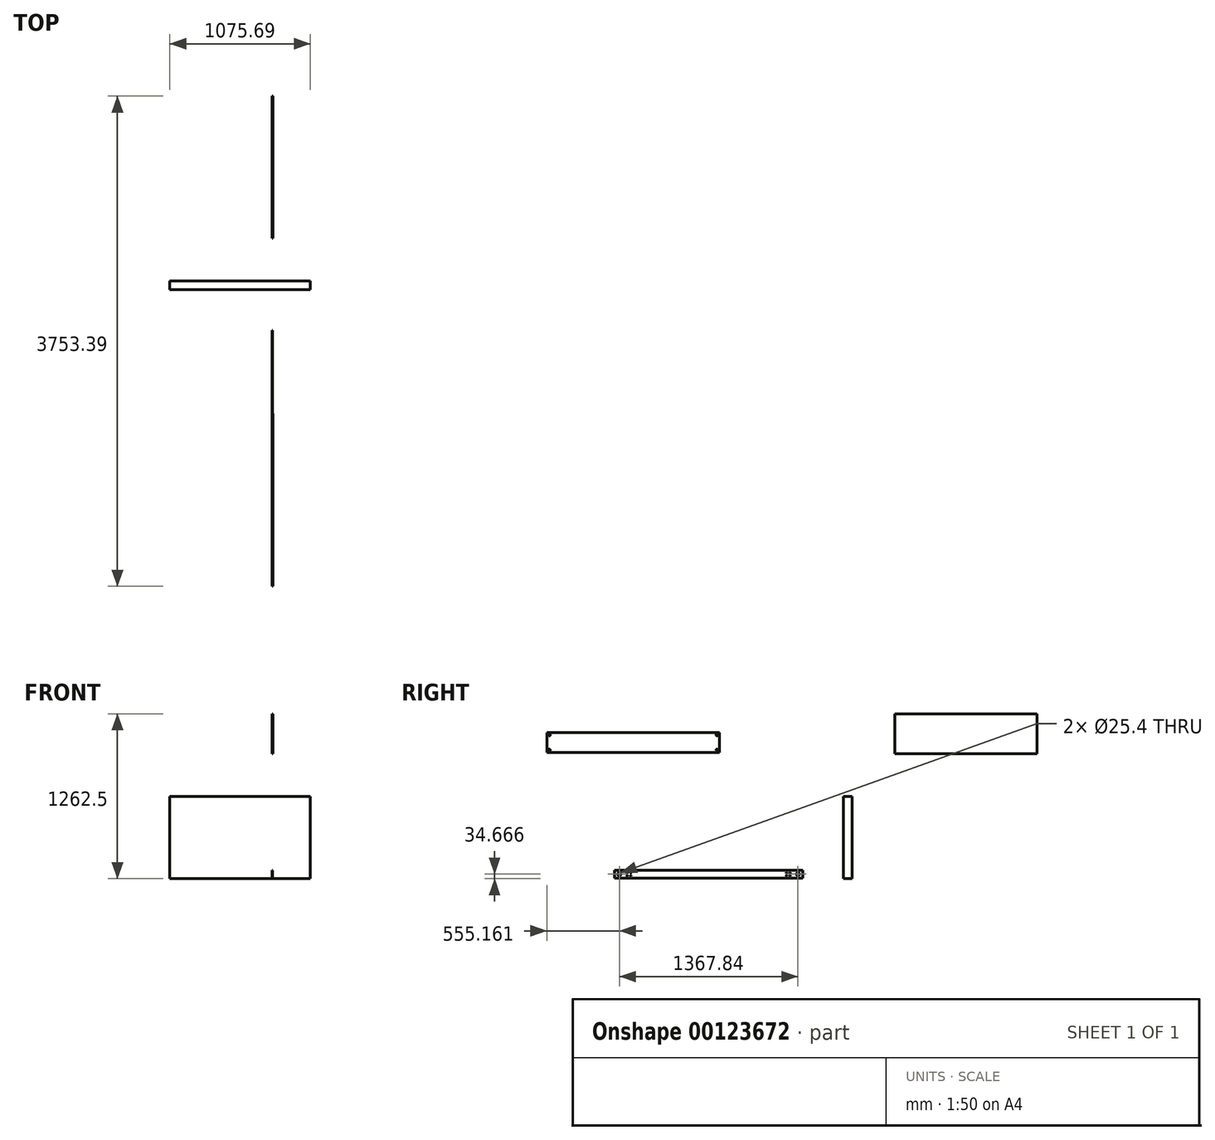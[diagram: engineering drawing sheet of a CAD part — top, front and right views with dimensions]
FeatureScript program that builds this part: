
annotation { "Feature Type Name" : "Feature", "Feature Type Description" : "" }
export const myFeature = defineFeature(function(context is Context, id is Id, definition is map)
    precondition{}
    {
        {
            var Q0;
            Q0=qCreatedBy(makeId("Front.planeOp"),FACE);
            var sketch = newSketch(context, id + "F0", { "sketchPlane" : qUnion([Q0])});
            skLineSegment(sketch, "E0.bottom", {"start": v(-783.94, 247.8) * mm, "end": v(291.75, 247.8) * mm});
            skLineSegment(sketch, "E0.top", {"start": v(-783.94, -380.85) * mm, "end": v(291.75, -380.85) * mm});
            skLineSegment(sketch, "E0.left", {"start": v(-783.94, 247.8) * mm, "end": v(-783.94, -380.85) * mm});
            skLineSegment(sketch, "E0.right", {"start": v(291.75, 247.8) * mm, "end": v(291.75, -380.85) * mm});
            skSolve(sketch);
        }
        {
            var Q0;
            Q0=makeQuery(id+"F0.imprint","IMPRINT",FACE,{"disambiguationData":[TD([[makeQuery(id+"F0.imprint","IMPRINT",EDGE,{"derivedFrom":sQuery(id+"F0.wireOp",EDGE,"E0.bottom")}),-1.0]])]});
            extrude(context, id + "F1", {"entities" : qUnion([Q0]), "depth" : 67.3 * mm});
        }
        {
            var Q0;
            Q0=qCreatedBy(makeId("Right.planeOp"),FACE);
            var sketch = newSketch(context, id + "F2", { "sketchPlane" : qUnion([Q0])});
            skLineSegment(sketch, "E1.bottom", {"start": v(325.72, 881.65) * mm, "end": v(1414.1, 881.65) * mm});
            skLineSegment(sketch, "E1.top", {"start": v(325.72, 576.85) * mm, "end": v(1414.1, 576.85) * mm});
            skLineSegment(sketch, "E1.left", {"start": v(325.72, 881.65) * mm, "end": v(325.72, 576.85) * mm});
            skLineSegment(sketch, "E1.right", {"start": v(1414.1, 881.65) * mm, "end": v(1414.1, 576.85) * mm});
            skSolve(sketch);
        }
        {
            var Q0;
            Q0=makeQuery(id+"F2.imprint","IMPRINT",FACE,{"disambiguationData":[TD([[makeQuery(id+"F2.imprint","IMPRINT",EDGE,{"derivedFrom":sQuery(id+"F2.wireOp",EDGE,"E1.bottom")}),-1.0]])]});
            extrude(context, id + "F3", {"entities" : qUnion([Q0]), "depth" : 6.35 * mm});
        }
        {
            var Q0;
            Q0=qCreatedBy(makeId("Right.planeOp"),FACE);
            var sketch = newSketch(context, id + "F4", { "sketchPlane" : qUnion([Q0])});
            skLineSegment(sketch, "E2.bottom", {"start": v(-2339.28, 737.4) * mm, "end": v(-1018.48, 737.4) * mm});
            skLineSegment(sketch, "E2.top", {"start": v(-2339.28, 585) * mm, "end": v(-1018.48, 585) * mm});
            skLineSegment(sketch, "E2.left", {"start": v(-2339.28, 737.4) * mm, "end": v(-2339.28, 585) * mm});
            skLineSegment(sketch, "E2.right", {"start": v(-1018.48, 737.4) * mm, "end": v(-1018.48, 585) * mm});
            skLineSegment(sketch, "E3", {"start": v(-1678.88, 737.4) * mm, "end": v(-1678.88, 585) * mm, "construction": true});
            skLineSegment(sketch, "E4", {"start": v(-1678.88, 585) * mm, "end": v(-2339.28, 661.2) * mm, "construction": true});
            skLineSegment(sketch, "E5", {"start": v(-2339.28, 661.2) * mm, "end": v(-1018.48, 661.2) * mm, "construction": true});
            skCircle(sketch, "E6", {"center": v(-2320.23, 718.34) * mm, "radius": 6.35 * mm});
            skCircle(sketch, "E7.MirrorC", {"center": v(-1037.53, 718.34) * mm, "radius": 6.35 * mm});
            skCircle(sketch, "E8.MirrorC", {"center": v(-2320.23, 604.04) * mm, "radius": 6.35 * mm});
            skCircle(sketch, "E9.MirrorC", {"center": v(-1037.53, 604.04) * mm, "radius": 6.35 * mm});
            skSolve(sketch);
        }
        {
            var Q0;
            Q0=makeQuery(id+"F4.imprint","IMPRINT",FACE,{"disambiguationData":[TD([[makeQuery(id+"F4.imprint","IMPRINT",EDGE,{"derivedFrom":sQuery(id+"F4.wireOp",EDGE,"E2.bottom")}),-1.0]])]});
            extrude(context, id + "F5", {"entities" : qUnion([Q0]), "depth" : 6.35 * mm});
        }
        {
            var Q0;
            Q0=qCreatedBy(makeId("Right.planeOp"),FACE);
            var sketch = newSketch(context, id + "F6", { "sketchPlane" : qUnion([Q0])});
            skLineSegment(sketch, "E10.bottom", {"start": v(-1822.22, -315.8) * mm, "end": v(-378.18, -315.8) * mm});
            skLineSegment(sketch, "E10.top", {"start": v(-1822.22, -378.7) * mm, "end": v(-378.18, -378.7) * mm});
            skLineSegment(sketch, "E10.left", {"start": v(-1822.22, -315.8) * mm, "end": v(-1822.22, -378.7) * mm});
            skLineSegment(sketch, "E10.right", {"start": v(-378.18, -315.8) * mm, "end": v(-378.18, -378.7) * mm});
            skCircle(sketch, "E11", {"center": v(-1784.12, -346.18) * mm, "radius": 12.7 * mm});
            skLineSegment(sketch, "E12", {"start": v(-1822.22, -347.25) * mm, "end": v(-378.18, -347.25) * mm, "construction": true});
            skCircle(sketch, "E13", {"center": v(-1710.12, -347.25) * mm, "radius": 18.22 * mm, "construction": true});
            skCircle(sketch, "E14", {"center": v(-1723.48, -334.86) * mm, "radius": 3.18 * mm});
            skLineSegment(sketch, "E15", {"start": v(-1710.12, -329.03) * mm, "end": v(-1710.12, -365.48) * mm, "construction": true});
            skCircle(sketch, "E16.MirrorC", {"center": v(-1696.76, -334.86) * mm, "radius": 3.18 * mm});
            skCircle(sketch, "E17.MirrorC", {"center": v(-1696.76, -359.65) * mm, "radius": 3.18 * mm});
            skCircle(sketch, "E18.MirrorC", {"center": v(-1723.48, -359.65) * mm, "radius": 3.18 * mm});
            skLineSegment(sketch, "E19", {"start": v(-1100.2, -315.8) * mm, "end": v(-1100.2, -378.7) * mm, "construction": true});
            skCircle(sketch, "E20.MirrorC", {"center": v(-416.28, -346.18) * mm, "radius": 12.7 * mm});
            skCircle(sketch, "E21.MirrorC", {"center": v(-476.92, -334.86) * mm, "radius": 3.18 * mm});
            skCircle(sketch, "E22.MirrorC", {"center": v(-503.64, -334.86) * mm, "radius": 3.18 * mm});
            skCircle(sketch, "E23.MirrorC", {"center": v(-476.92, -359.65) * mm, "radius": 3.18 * mm});
            skCircle(sketch, "E24.MirrorC", {"center": v(-503.64, -359.65) * mm, "radius": 3.18 * mm});
            skSolve(sketch);
        }
        {
            var Q0;
            Q0=makeQuery(id+"F6.imprint","IMPRINT",FACE,{"disambiguationData":[TD([[makeQuery(id+"F6.imprint","IMPRINT",EDGE,{"derivedFrom":sQuery(id+"F6.wireOp",EDGE,"E10.bottom")}),-1.0]])]});
            extrude(context, id + "F7", {"entities" : qUnion([Q0]), "depth" : 3.17 * mm});
        }
    });
